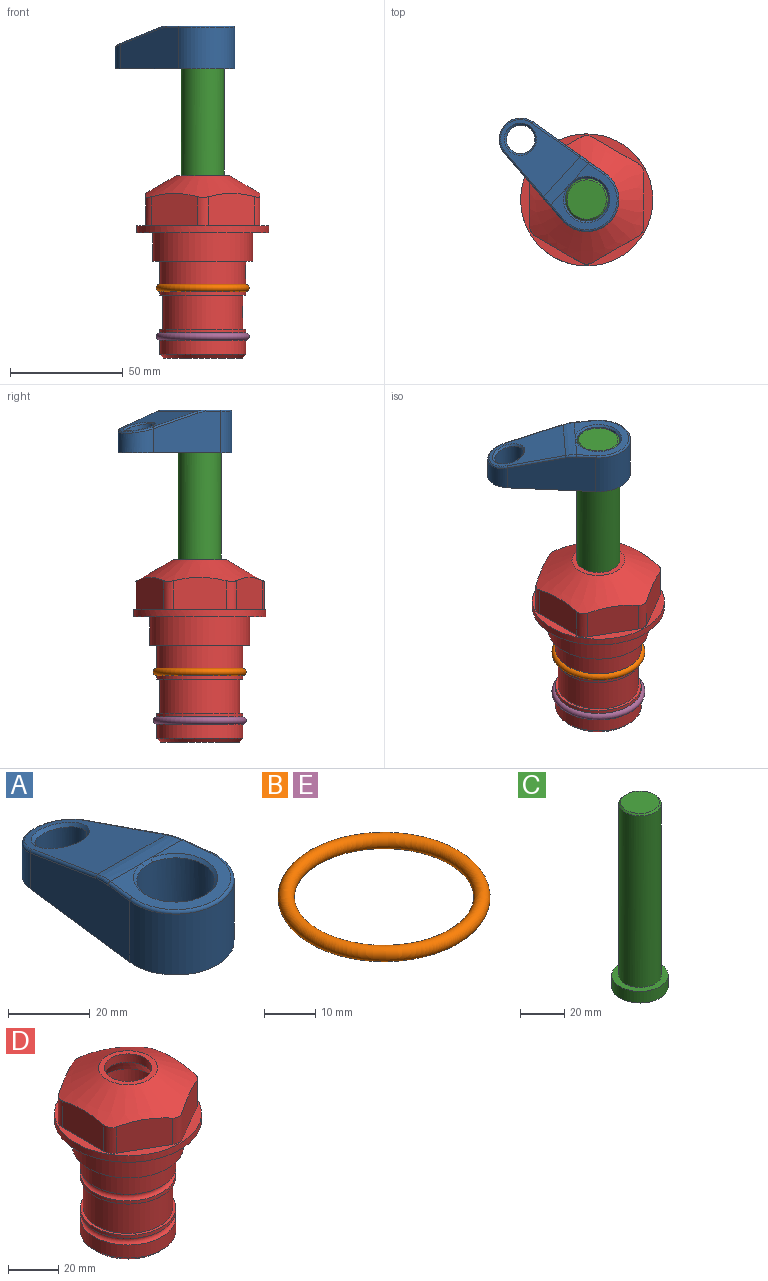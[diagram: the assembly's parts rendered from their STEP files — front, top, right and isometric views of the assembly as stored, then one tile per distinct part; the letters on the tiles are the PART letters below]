
ASSEMBLY  parts=5 mates=4
PART A: 31 faces, bbox 31.7x65.5x19.8 mm
  f0: plane 39.12x18.26mm, normal (0.99,0.12,0), area 612.2mm2, adj f1,f4,f7,f11,f13,f15
  f1: cylinder r=9.53mm len=18.91mm, axis (0,0,-1), area 296.1mm2, adj f0,f2,f7,f17
  f2: plane 39.12x18.26mm, normal (-0.99,0.12,0), area 612.2mm2, adj f1,f4,f7,f12,f14,f16
  f3: cylinder r=6.35mm len=12.7mm, axis (0,0,-1), area 362.4mm2, adj f7,f18
  f4: cylinder r=14.29mm len=28.58mm, axis (0,0,-1), area 882.2mm2, adj f0,f2,f7,f10
  f5: cylinder r=9.53mm len=19.05mm, axis (0,0,-1), area 1092.6mm2, adj f7,f19,f20
  f6: plane 26.99x23.69mm, normal (0,0,1), area 216.2mm2, adj f9,f10,f11,f12,f19
  f7: plane 63.5x28.58mm, normal (0,0,-1), area 661.8mm2, adj f0,f1,f2,f3,f4,f5,f22,f23
  f8: plane 33.52x23.6mm, normal (0,0.26,0.97), area 486mm2, adj f9,f15,f16,f17,f18
  f9: cylinder r=19.05mm len=24.72mm, axis (1,0,0), area 120.4mm2, adj f6,f8,f13,f14,f20
  f10: torus R=13.49mm, axis (0,0,1), area 59mm2, adj f4,f6,f11,f12
  f11: cylinder r=0.79mm len=8.67mm, axis (0.12,-0.99,0), area 10.8mm2, adj f0,f6,f10,f13
  f12: cylinder r=0.79mm len=8.67mm, axis (0.12,0.99,0), area 10.8mm2, adj f2,f6,f10,f14
  f13: bspline ~4.95x1.42mm, area 6.1mm2, adj f0,f9,f11,f15
  f14: bspline ~4.95x1.42mm, area 6.1mm2, adj f2,f9,f12,f16
  f15: cylinder r=0.79mm len=25.95mm, axis (0.12,-0.96,0.26), area 32.9mm2, adj f0,f8,f13,f17
  f16: cylinder r=0.79mm len=25.95mm, axis (0.12,0.96,-0.26), area 32.9mm2, adj f2,f8,f14,f17
  f17: bspline ~18.91x8.38mm, area 30mm2, adj f1,f8,f15,f16
  f18: bspline ~14.29x14.29mm, area 48.3mm2, adj f3,f8
  f19: cone r=9.53mm half-angle=45deg, axis (0,0,1), area 66.5mm2, adj f5,f6,f20
  f20: bspline ~3.22x0.96mm, area 3.5mm2, adj f5,f9,f19
  f21: plane 2.75x2.72mm, normal (0,0,-1), area 2.9mm2, adj f23,f25,f28
  f22: plane 23.05x15.88mm, normal (-0.99,-0.12,0), area 323.6mm2, adj f7,f25,f26,f27,f28,f29
  f23: plane 23.05x15.88mm, normal (0.99,-0.12,0), area 323.6mm2, adj f7,f21,f25,f27,f28,f30
  f24: cylinder r=9.53mm len=10.69mm, axis (0,0,-1), area 114.7mm2, adj f7,f27,f29,f30
  f25: cylinder r=12.7mm len=20.59mm, axis (0,0,-1), area 381.1mm2, adj f7,f21,f22,f23,f26,f28
  f26: plane 2.75x2.72mm, normal (0,0,-1), area 2.9mm2, adj f22,f25,f28
  f27: plane 19.72x18.37mm, normal (0,-0.26,-0.97), area 291.8mm2, adj f22,f23,f24,f28,f29,f30
  f28: cylinder r=15.88mm len=19.92mm, axis (1,0,0), area 54.8mm2, adj f21,f22,f23,f25,f26,f27
  f29: cylinder r=1.59mm len=11mm, axis (0,0,-1), area 34.7mm2, adj f7,f22,f24,f27
  f30: cylinder r=1.59mm len=11mm, axis (0,0,-1), area 34.7mm2, adj f7,f23,f24,f27
PART B: 1 faces, bbox 44.7x44.7x3.2 mm
  f0: torus R=19.05mm, axis (0,0,1), area 1193.9mm2
PART C: 6 faces, bbox 25.4x25.4x101.6 mm
  f0: plane 17.46x17.46mm, normal (0,0,1), area 239.5mm2, adj f5
  f1: plane 25.4x25.4mm, normal (0,0,-1), area 506.7mm2, adj f2
  f2: cylinder r=12.7mm len=25.4mm, axis (0,0,1), area 506.7mm2, adj f1,f3
  f3: plane 25.4x25.4mm, normal (0,0,1), area 221.7mm2, adj f2,f4
  f4: cylinder r=9.53mm len=94.46mm, axis (0,0,1), area 5653mm2, adj f3,f5
  f5: cone r=8.73mm half-angle=45deg, axis (0,0,-1), area 64.4mm2, adj f0,f4
PART D: 36 faces, bbox 58.7x58.7x81 mm
  f0: cylinder r=17.78mm len=35.56mm, axis (0,0,1), area 1670.8mm2, adj f23,f24,f31
  f1: cylinder r=19.05mm len=38.1mm, axis (0,0,1), area 1191.9mm2, adj f26,f27,f30
  f2: plane 58.66x58.66mm, normal (0,0,-1), area 1150.6mm2, adj f3,f28
  f3: cylinder r=29.33mm len=58.66mm, axis (0,0,-1), area 585.1mm2, adj f2,f4
  f4: plane 58.66x58.66mm, normal (0,0,1), area 475.9mm2, adj f3,f5,f6,f7,f8,f9,f10,f11
  f5: plane 20.32x14.34mm, normal (-0.5,0.87,0), area 324.4mm2, adj f4,f15,f16,f17
  f6: plane 20.32x14.34mm, normal (0.5,0.87,0), area 324.4mm2, adj f4,f14,f15,f17
  f7: plane 23.48x14.34mm, normal (1,0,0), area 324.4mm2, adj f4,f13,f14,f17
  f8: plane 20.32x14.34mm, normal (0.5,-0.87,0), area 324.4mm2, adj f4,f12,f13,f17
  f9: plane 20.32x14.34mm, normal (-0.5,-0.87,0), area 324.4mm2, adj f4,f11,f12,f17
  f10: plane 23.48x14.34mm, normal (-1,0,0), area 324.4mm2, adj f4,f11,f16,f17
  f11: cylinder r=5.08mm len=12.85mm, axis (0,0,-1), area 67.2mm2, adj f4,f9,f10,f17
  f12: cylinder r=5.08mm len=12.85mm, axis (0,0,-1), area 67.2mm2, adj f4,f8,f9,f17
  f13: cylinder r=5.08mm len=12.85mm, axis (0,0,-1), area 67.2mm2, adj f4,f7,f8,f17
  f14: cylinder r=5.08mm len=12.85mm, axis (0,0,-1), area 67.2mm2, adj f4,f6,f7,f17
  f15: cylinder r=5.08mm len=12.85mm, axis (0,0,-1), area 67.2mm2, adj f4,f5,f6,f17
  f16: cylinder r=5.08mm len=12.85mm, axis (0,0,-1), area 67.2mm2, adj f4,f5,f10,f17
  f17: cone r=11.73mm half-angle=60deg, axis (0,0,-1), area 2071.8mm2, adj f5,f6,f7,f8,f9,f10,f11,f12
  f18: plane 23.46x23.46mm, normal (0,0,1), area 147.4mm2, adj f17,f35
  f19: plane 34.93x34.93mm, normal (0,0,-1), area 958mm2, adj f29
  f20: cylinder r=19.05mm len=38.1mm, axis (0,0,1), area 760.1mm2, adj f21,f29
  f21: torus R=19.05mm, axis (0,0,1), area 565.3mm2, adj f20,f22
  f22: cylinder r=19.05mm len=38.1mm, axis (0,0,1), area 190mm2, adj f21,f23
  f23: plane 38.1x38.1mm, normal (0,0,1), area 146.9mm2, adj f0,f22
  f24: plane 38.1x38.1mm, normal (0,0,-1), area 146.9mm2, adj f0,f25
  f25: cylinder r=19.05mm len=38.1mm, axis (0,0,1), area 190mm2, adj f24,f26
  f26: torus R=19.05mm, axis (0,0,1), area 565.3mm2, adj f1,f25
  f27: plane 44.45x44.45mm, normal (0,0,-1), area 411.7mm2, adj f1,f28
  f28: cylinder r=22.23mm len=44.45mm, axis (0,0,1), area 1773.5mm2, adj f2,f27
  f29: cone r=19.05mm half-angle=45deg, axis (0,0,1), area 257.5mm2, adj f19,f20
  f30: cylinder r=3.17mm len=6.75mm, axis (-1,0,0), area 128mm2, adj f1,f33
  f31: cylinder r=3.17mm len=6.35mm, axis (-1,0,0), area 102.5mm2, adj f0,f33
  f32: plane 25.4x25.4mm, normal (0,0,1), area 506.7mm2, adj f33
  f33: cylinder r=12.7mm len=66.42mm, axis (0,0,-1), area 5236.2mm2, adj f30,f31,f32,f34
  f34: cone r=9.53mm half-angle=30deg, axis (0,0,-1), area 443.4mm2, adj f33,f35
  f35: cylinder r=9.53mm len=19.05mm, axis (0,0,-1), area 240.9mm2, adj f18,f34
PART E: same geometry as B
PLACE A rot(axis=(0,0,1),47.7deg) t=(0,0,28.35)mm
PLACE B at identity
PLACE C rot(axis=(0,0,1),47.7deg) t=(0,0,27.55)mm
PLACE D at identity fixed
PLACE E t=(0,0,-21.59)mm
MATE fastened B.f0 <-> D.f0  axis (0,0,1) through (0,0,-24.51)mm
MATE cylindrical D.f0 <-> C.f2  axis (0,0,1) through (0,0,-50.55)mm
MATE fastened E.f0 <-> D.f0  axis (0,0,1) through (0,0,-46.1)mm
MATE fastened C.f2 <-> A.f4  axis (0,0,1) through (0,0,91.05)mm
